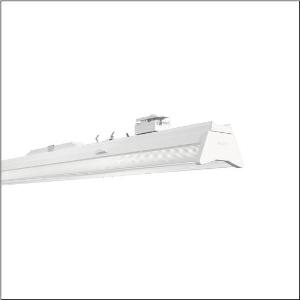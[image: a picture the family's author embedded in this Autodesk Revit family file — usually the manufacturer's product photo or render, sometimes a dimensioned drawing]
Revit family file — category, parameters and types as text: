
# Revit family: licross_r__11_performance_mo_51tm16dn445g_758e
name_source: partatom
category: Lighting Fixtures
units: mm (PartAtom-declared; Revit-internal decimal feet)

## family parameters
Cut with Voids When Loaded = No
Host = Face
Light Source = No
Part Type = Normal
Room Calculation Point = No
Round Connector Dimension = Use Diameter
Shared = No

## types (1)
- --- (1 x LED, 4520 lm, 24.3 W, 4000K)
    Apparent Load = 24 VA
    CIE Flux Codes = 66 88 96 79 100
    Color Rendering = 80
    Color Temperature = 4000K
    Default Elevation = 1800 mm
    Description = Licross® 11 Performance MO, luminaire insert, of sheet steel, galvanised, coil coated, white, length: 1.500mm, width: 120mm, height: 123mm, LED rated luminous flux: 4.520lm, light colour: 840, control gear: DALI 2, with plug, 5-pole, with phase selection, mains connection: 220..240V, AC, 50/60Hz, rated input power: 24W, halogen-free wiring, primary light control with lens, of plastic, primary optical cover: cover, of PMMA, CAT 2 (L<= 3000cd/m²), light emission: direct/indirect distribution, primary light characteristic: symmetric, protection rating (complete): IP40, insulation class (complete): insulation class I (protective earthing), certification: CE, ENEC, VDE, UKCA, protection symbol: D if used in an environment without relevant dust loads with corresponding accessories, impact resistance: IK06, permissible ambient temperature for indoor applications: -25..+45°C, corresponds to IFS (International Featured Standards) requirements for safety and quality in the food industry, reducing of maximum allowable ambient temperature of 5°C with ceiling mounting, LABS conformity tested according to VDMA 24364:2018-05, packaging unit: 1 piece
    Height = 114 mm
    Lamp = 1 x LED
    Lamp Light Flux = 4520 lm
    Lamp Power = 24.3 W
    Lamp count = 1
    Length = 1500 mm
    Luminous efficacy = 186 lm/W
    Manufacturer = Siteco
    ModVariant = No
    Model = 51TM16DN445G
    Mounting Place = Ceiling
    Mounting Type = Pendant
    Number of Poles = 1
    OnlyDefault = Yes
    Power Factor = 1
    Product Name = Licross® 11 Performance MO
    Product group = luminaire insert
    ProductGroupID = 901
    Protection Class = Protection class I
    Protection Degree = IP 40
    RLX_Detail_Level = 1
    RLX_Emergency_Light_Flux = 0 lm
    RLX_Emergency_Type = 0
    RLX_Emergency_Type_DB = No
    RlxData = <blob elided: 33793 chars, md5=fba1728c>
    Socket = socket
    Standby Power = 0 W
    System Light Flux = 4520 lm
    System Power = 24 W
    Type Comments = factory setting: luminous flux: 100 % | dim-lin: 254 | 161 mA
    Type Image = l_1256138.jpg
    URL = http://relux.com
    VarID = @adj_007027
    Voltage = 0 V
    Weight = 0.00 kg
    Width = 120 mm

## geometry (parser evidence)
native form markers: Blend x4, Sweep x13
no freeform markers — native parametric forms only
